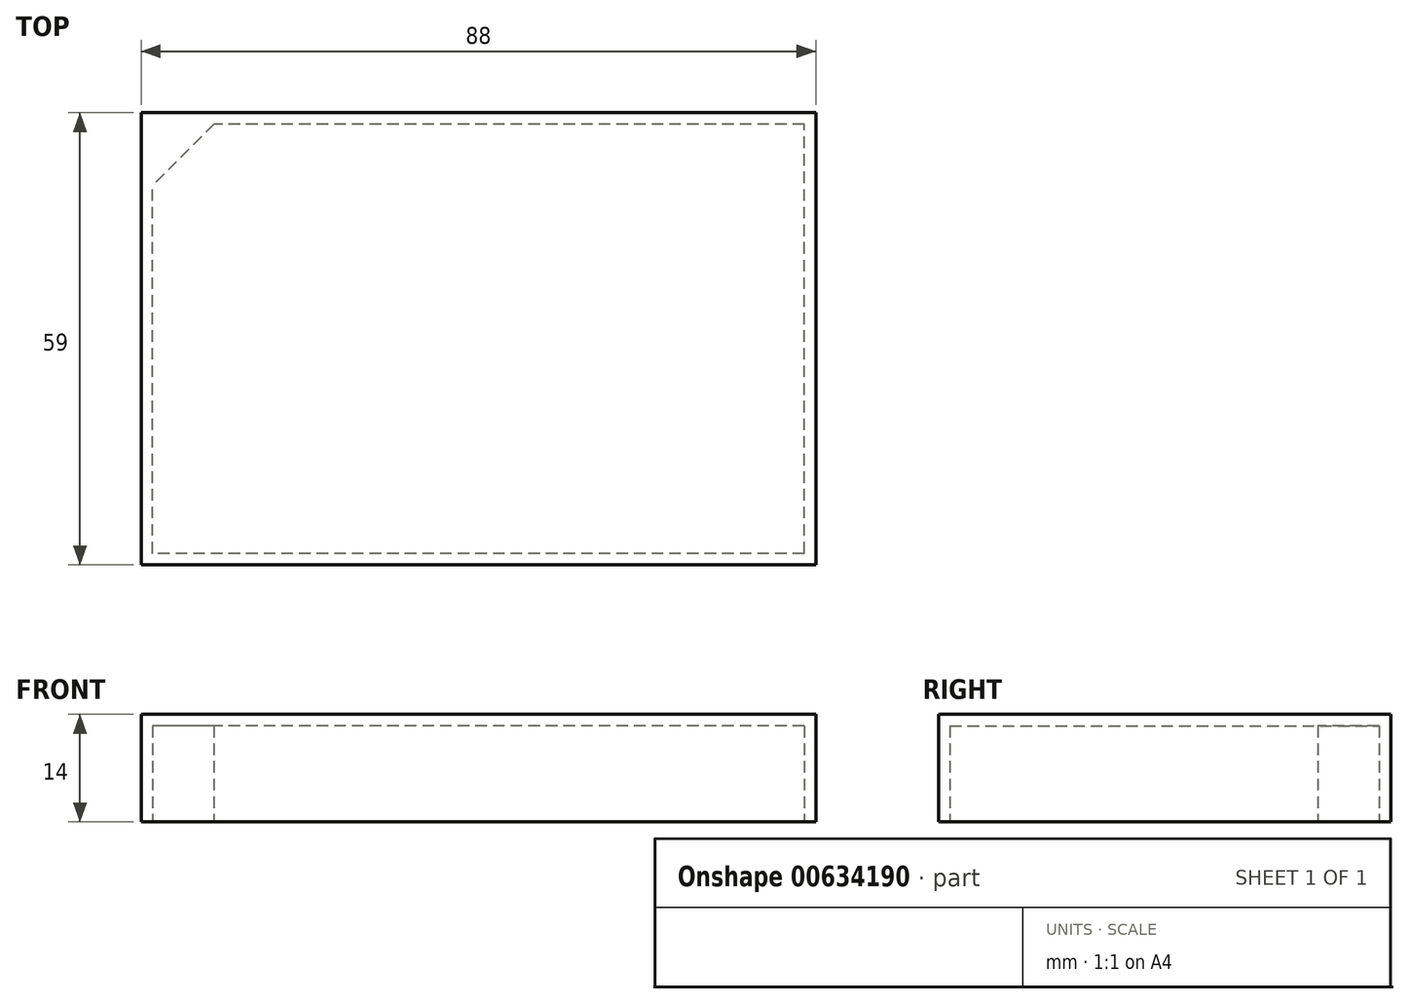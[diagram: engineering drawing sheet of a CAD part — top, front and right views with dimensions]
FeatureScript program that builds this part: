
annotation { "Feature Type Name" : "Feature", "Feature Type Description" : "" }
export const myFeature = defineFeature(function(context is Context, id is Id, definition is map)
    precondition{}
    {
        {
            var Q0;
            Q0=qCreatedBy(makeId("Top.planeOp"),FACE);
            var sketch = newSketch(context, id + "F0", { "sketchPlane" : qUnion([Q0])});
            skLineSegment(sketch, "E0.bottom", {"start": v(42.5, -28) * mm, "end": v(-42.5, -28) * mm});
            skLineSegment(sketch, "E0.top", {"start": v(42.5, 28) * mm, "end": v(-42.5, 28) * mm});
            skLineSegment(sketch, "E0.left", {"start": v(42.5, -28) * mm, "end": v(42.5, 28) * mm});
            skLineSegment(sketch, "E0.right", {"start": v(-42.5, -28) * mm, "end": v(-42.5, 28) * mm});
            skPoint(sketch, "E0.middle", {"position": v(0, 0) * mm});
            skLineSegment(sketch, "E1", {"start": v(-42.5, 28) * mm, "end": v(-34.5, 28) * mm});
            skLineSegment(sketch, "E2", {"start": v(-34.5, 28) * mm, "end": v(-42.5, 20) * mm});
            skLineSegment(sketch, "E3", {"start": v(-42.5, 20) * mm, "end": v(-42.5, 28) * mm});
            skSolve(sketch);
        }
        {
            var Q0;
            Q0=qCreatedBy(makeId("Top.planeOp"),FACE);
            var sketch = newSketch(context, id + "F1", { "sketchPlane" : qUnion([Q0])});
            skLineSegment(sketch, "E4.bottom", {"start": v(44, 29.5) * mm, "end": v(-44, 29.5) * mm});
            skLineSegment(sketch, "E4.top", {"start": v(44, -29.5) * mm, "end": v(-44, -29.5) * mm});
            skLineSegment(sketch, "E4.left", {"start": v(44, 29.5) * mm, "end": v(44, -29.5) * mm});
            skLineSegment(sketch, "E4.right", {"start": v(-44, 29.5) * mm, "end": v(-44, -29.5) * mm});
            skPoint(sketch, "E4.middle", {"position": v(0, 0) * mm});
            skSolve(sketch);
        }
        {
            var Q0;
            Q0 = qSketchRegion(id + "F1", true);
            extrude(context, id + "F2", {"entities" : qUnion([Q0]), "depth" : 14 * mm, "offsetDistance" : 25 * mm});
        }
        {
            var Q0;
            Q0=makeQuery(id+"F0.imprint","IMPRINT",FACE,{"disambiguationData":[TD([[makeQuery(id+"F0.imprint","IMPRINT",EDGE,{"derivedFrom":sQuery(id+"F0.wireOp",EDGE,"E0.bottom")}),-1.0]])]});
            extrude(context, id + "F3", {"entities" : qUnion([Q0]), "operationType" : NewBodyOperationType.REMOVE, "oppositeDirection" : true, "depth" : -12.5 * mm, "offsetDistance" : 25 * mm});
        }
    });
